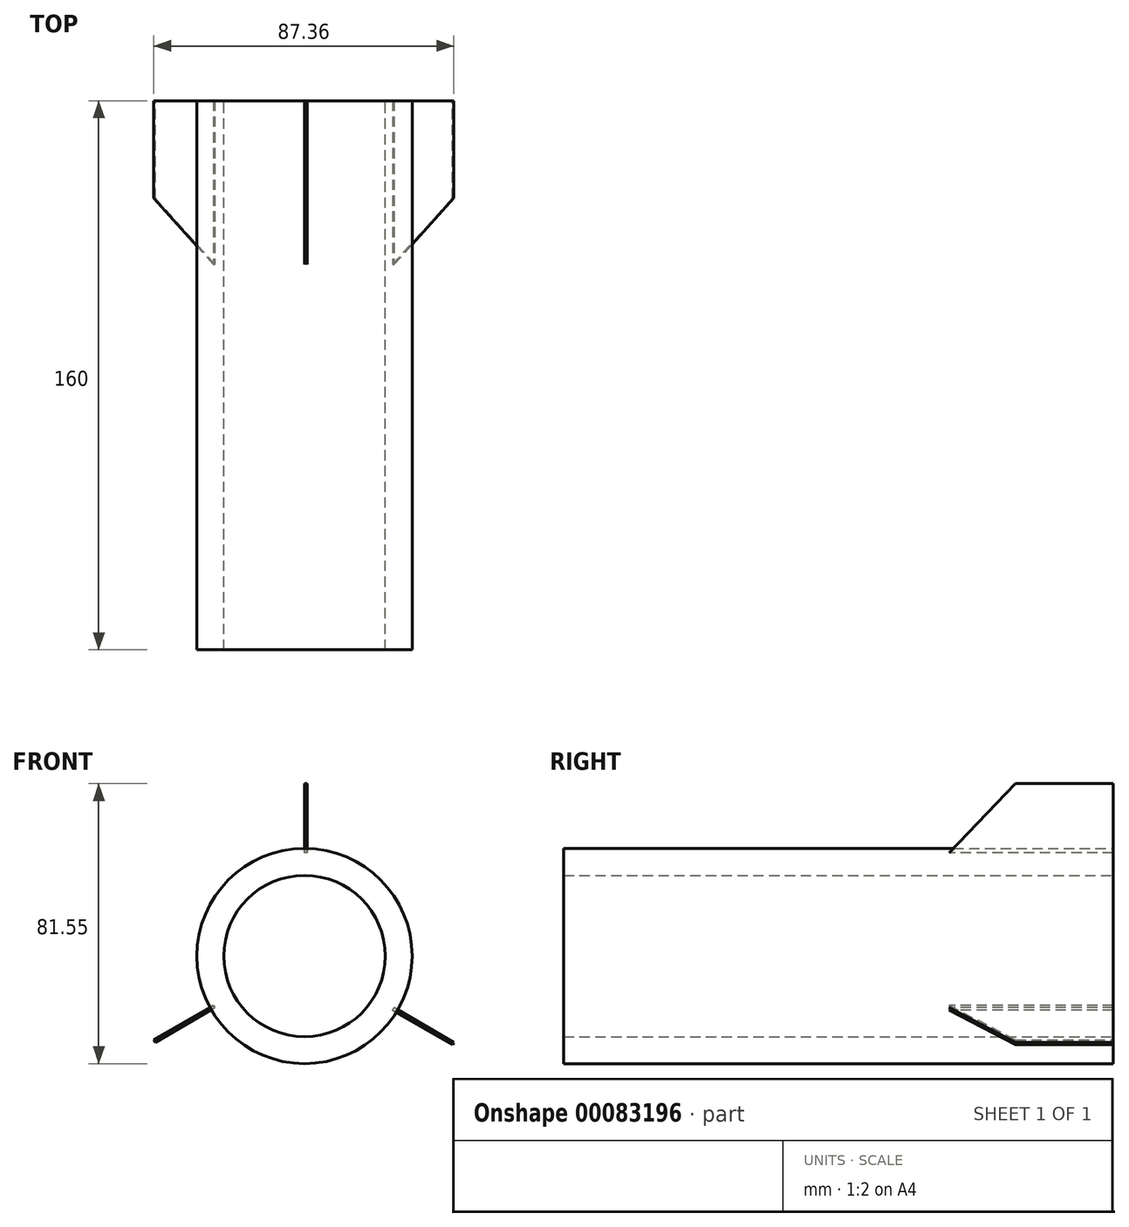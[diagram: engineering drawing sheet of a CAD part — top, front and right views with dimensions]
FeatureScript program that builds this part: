
annotation { "Feature Type Name" : "Feature", "Feature Type Description" : "" }
export const myFeature = defineFeature(function(context is Context, id is Id, definition is map)
    precondition{}
    {
        {
            var Q0;
            Q0=qCreatedBy(makeId("Front.planeOp"),FACE);
            var sketch = newSketch(context, id + "F0", { "sketchPlane" : qUnion([Q0])});
            skCircle(sketch, "E0", {"center": v(0, 0) * mm, "radius": 23.5 * mm});
            skCircle(sketch, "E1", {"center": v(0, 0) * mm, "radius": 31.34 * mm});
            skSolve(sketch);
        }
        {
            var Q0;
            Q0=makeQuery(id+"F0.imprint","IMPRINT",FACE,{"disambiguationData":[TD([[makeQuery(id+"F0.imprint","IMPRINT",EDGE,{"derivedFrom":sQuery(id+"F0.wireOp",EDGE,"E0")}),-1.0]])]});
            extrude(context, id + "F1", {"entities" : qUnion([Q0]), "depth" : 160 * mm});
        }
        {
            var Q0;
            Q0=qCreatedBy(makeId("Right.planeOp"),FACE);
            var sketch = newSketch(context, id + "F2", { "sketchPlane" : qUnion([Q0])});
            skLineSegment(sketch, "E2", {"start": v(0, 30.13) * mm, "end": v(-47.72, 30.13) * mm});
            skLineSegment(sketch, "E3", {"start": v(-47.72, 30.13) * mm, "end": v(-28.4, 50.21) * mm});
            skLineSegment(sketch, "E4", {"start": v(-28.4, 50.21) * mm, "end": v(0, 50.21) * mm});
            skLineSegment(sketch, "E5", {"start": v(0, 50.21) * mm, "end": v(0, 30.13) * mm});
            skSolve(sketch);
        }
        {
            var Q0;
            Q0 = qSketchRegion(id + "F2", true);
            extrude(context, id + "F3", {"entities" : qUnion([Q0]), "depth" : 0.8 * mm});
        }
        {
            var Q0;
            Q0=makeQuery(id+"F3.opExtrude","SWEPT_BODY",BODY,{"disambiguationData":[OSD([sQuery(id+"F2.wireOp",EDGE,"E2"),sQuery(id+"F2.wireOp",EDGE,"E3"),sQuery(id+"F2.wireOp",EDGE,"E4"),sQuery(id+"F2.wireOp",EDGE,"E5")])]});
            var Q1;
            Q1=makeQuery(id+"F1.opExtrude","SWEPT_FACE",FACE,{"disambiguationData":[OSD([sQuery(id+"F0.wireOp",EDGE,"E1")])]});
            circularPattern(context, id + "F4", {"entities" : qUnion([Q0]), "axis" : qUnion([Q1]), "angle" : 360 * degree, "instanceCount" : 3, "equalSpace" : true});
        }
    });
